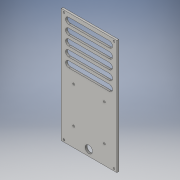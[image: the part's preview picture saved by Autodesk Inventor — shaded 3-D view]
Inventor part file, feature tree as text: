
AUTODESK INVENTOR PART (.ipt)
format: ipt  version: 2016 (Build 200138000, 138)  size: 155,136 bytes
history: native  units: mm
features: hole x3, sketch x3, extrude x2, mirror x2, pattern_linear x1
ambient origin geometry x8: Origin, YZ Plane, XZ Plane, XY Plane, X Axis, Y Axis, Z Axis, Center Point
bodies: Volumenkörper1 (feature_tree)
feature tree (11):
  extrude  "Extrusion1"  Depth=182.6mm
  hole  "Bohrung1"  [1 undecoded]
  extrude  "Extrusion2"  Depth=30.0mm
  pattern_linear  "Rechteckige Anordnung1"  Spacing1=75.0mm  [1 undecoded]
  hole  "Bohrung2"  [1 undecoded]
  mirror  "Spiegeln1"
  mirror  "Spiegeln2"
  hole  "Bohrung3"  [1 undecoded]
  sketch  "Skizze1"  dims[d0=88.6mm d1=182.6mm]
  sketch  "Skizze2"  dims[d2=3.0mm d3=0.0mm d5=49.0mm]
  sketch  "Skizze3"  dims[d6=58.0mm d7=30.0mm d8=3.0mm d9=6.0mm d10=4.0mm d11=2.0mm d12=90.0deg d13=2.5mm d14=0.0mm d15=75.0mm d16=10.0mm d18=5.0mm d19=5.0mm d20=5.0mm d21=10.0mm d22=0.0mm d23=50.0mm d25=15.0mm d26=4.4mm d27=3.4mm d28=3.0mm d29=6.0mm d30=4.0mm d31=2.0mm d32=90.0deg d33=8.0mm d34=20.594885mm d35=10.0mm d36=44.0mm d37=11.8mm d38=6.0mm d39=4.0mm d40=2.0mm d41=90.0deg d42=8.0mm d43=20.594885mm]
note: 4 required parameter values undecoded (feature->parameter linkage not recoverable at this tier; creation-order binding heuristic only, values carry confidence <= 0.55)
